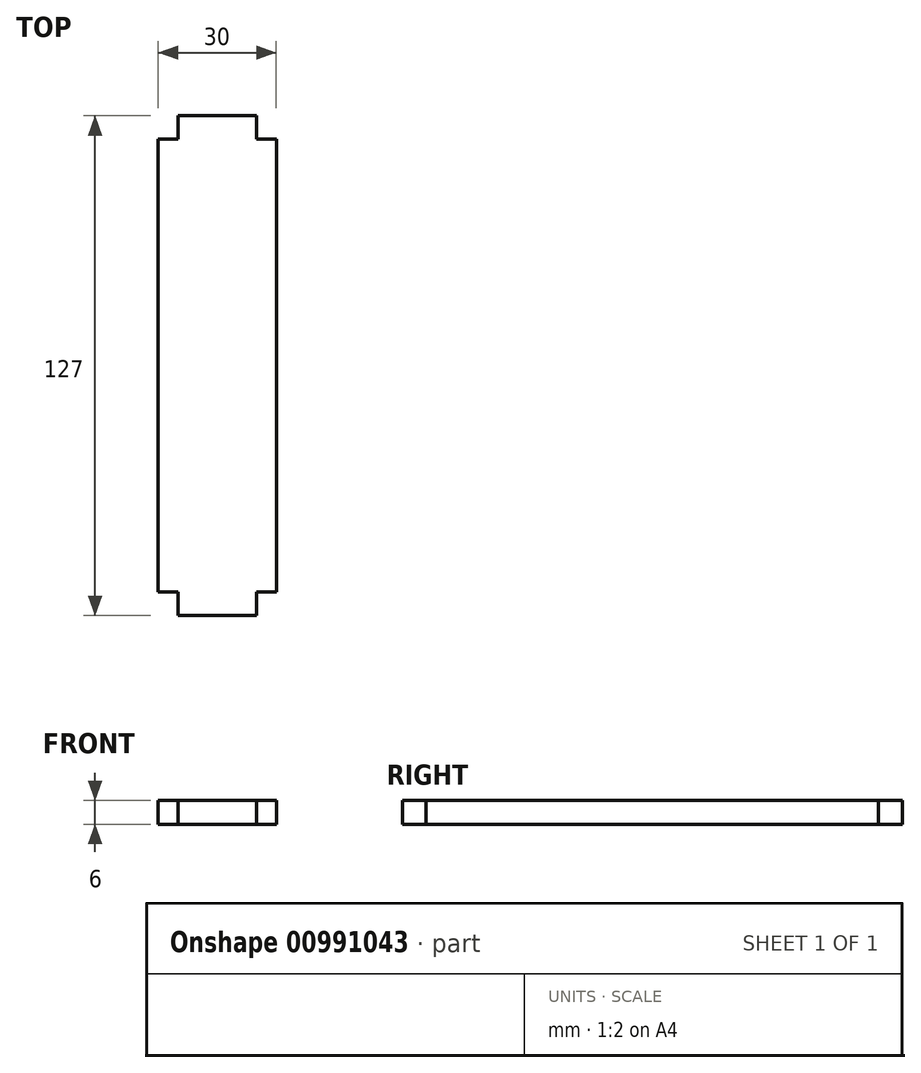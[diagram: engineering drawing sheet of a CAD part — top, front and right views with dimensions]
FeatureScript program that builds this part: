
annotation { "Feature Type Name" : "Feature", "Feature Type Description" : "" }
export const myFeature = defineFeature(function(context is Context, id is Id, definition is map)
    precondition{}
    {
        {
            var Q0;
            Q0=qCreatedBy(makeId("Top.planeOp"),FACE);
            var sketch = newSketch(context, id + "F0", { "sketchPlane" : qUnion([Q0])});
            skLineSegment(sketch, "E0.bottom", {"start": v(-34.2, -50.27) * mm, "end": v(-14.2, -50.27) * mm});
            skLineSegment(sketch, "E0.top", {"start": v(-34.2, 76.73) * mm, "end": v(-14.2, 76.73) * mm});
            skLineSegment(sketch, "E0.left", {"start": v(-39.2, -44.27) * mm, "end": v(-39.2, 70.73) * mm});
            skLineSegment(sketch, "E0.right", {"start": v(-9.2, -44.27) * mm, "end": v(-9.2, 70.73) * mm});
            skLineSegment(sketch, "E1", {"start": v(-34.2, -50.27) * mm, "end": v(-34.2, -44.27) * mm});
            skLineSegment(sketch, "E2", {"start": v(-34.2, -44.27) * mm, "end": v(-39.2, -44.27) * mm});
            skLineSegment(sketch, "E3.top", {"start": v(-39.2, 70.73) * mm, "end": v(-34.2, 70.73) * mm});
            skLineSegment(sketch, "E3.right", {"start": v(-34.2, 76.73) * mm, "end": v(-34.2, 70.73) * mm});
            skLineSegment(sketch, "E4.top", {"start": v(-9.2, 70.73) * mm, "end": v(-14.2, 70.73) * mm});
            skLineSegment(sketch, "E4.right", {"start": v(-14.2, 76.73) * mm, "end": v(-14.2, 70.73) * mm});
            skLineSegment(sketch, "E5.top", {"start": v(-9.2, -44.27) * mm, "end": v(-14.2, -44.27) * mm});
            skLineSegment(sketch, "E5.right", {"start": v(-14.2, -50.27) * mm, "end": v(-14.2, -44.27) * mm});
            skPoint(sketch, "E6.orphan", {"position": v(-39.2, -50.27) * mm});
            skSolve(sketch);
        }
        {
            var Q0;
            Q0 = qSketchRegion(id + "F0", true);
            extrude(context, id + "F1", {"entities" : qUnion([Q0]), "depth" : 6 * mm, "offsetDistance" : 25 * mm});
        }
    });
